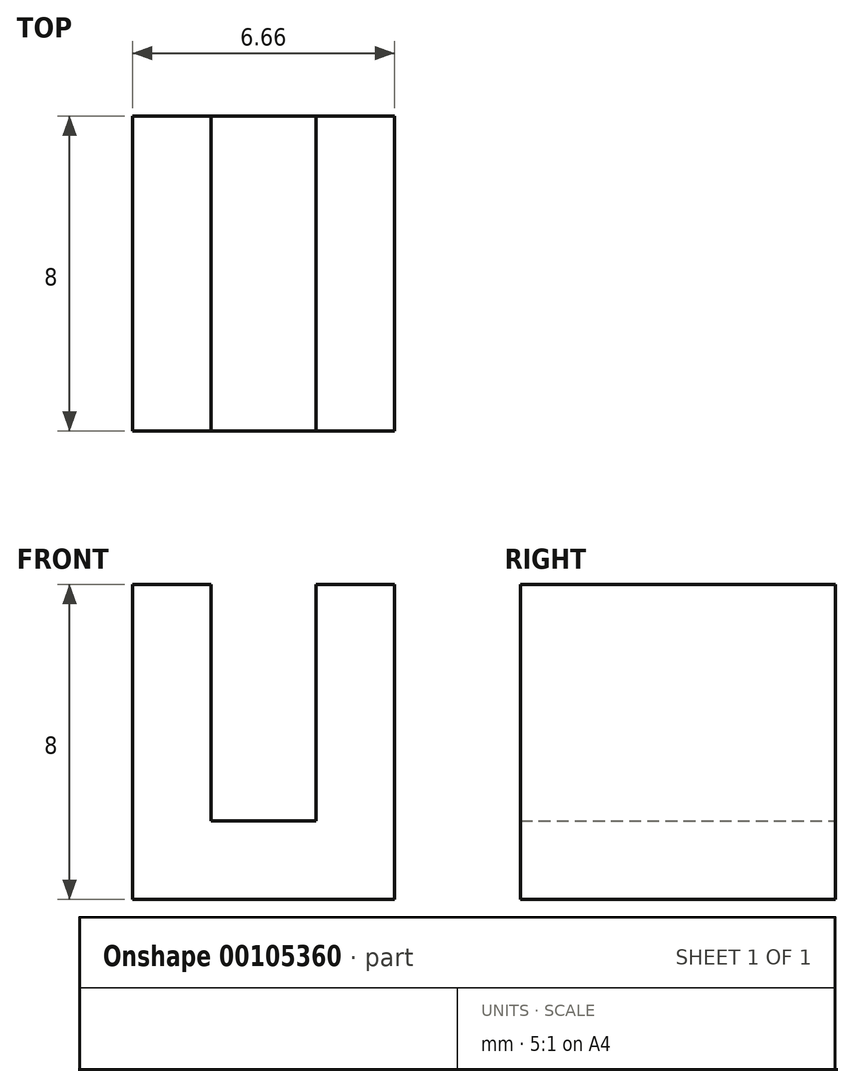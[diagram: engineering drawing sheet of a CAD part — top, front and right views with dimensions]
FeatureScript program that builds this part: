
annotation { "Feature Type Name" : "Feature", "Feature Type Description" : "" }
export const myFeature = defineFeature(function(context is Context, id is Id, definition is map)
    precondition{}
    {
        {
            var Q0;
            Q0=qCreatedBy(makeId("Front.planeOp"),FACE);
            var sketch = newSketch(context, id + "F0", { "sketchPlane" : qUnion([Q0])});
            skLineSegment(sketch, "E0", {"start": v(0, 0) * mm, "end": v(1.33, 0) * mm});
            skLineSegment(sketch, "E1", {"start": v(1.33, 0) * mm, "end": v(1.33, 6) * mm});
            skLineSegment(sketch, "E2", {"start": v(1.33, 6) * mm, "end": v(3.33, 6) * mm});
            skLineSegment(sketch, "E3", {"start": v(3.33, 6) * mm, "end": v(3.33, -2) * mm});
            skLineSegment(sketch, "E4", {"start": v(3.33, -2) * mm, "end": v(0, -2) * mm});
            skLineSegment(sketch, "E5.MirrorCS", {"start": v(-1.33, 6) * mm, "end": v(-3.33, 6) * mm});
            skLineSegment(sketch, "E6.MirrorCS", {"start": v(-3.33, 6) * mm, "end": v(-3.33, -2) * mm});
            skLineSegment(sketch, "E7.MirrorCS", {"start": v(-1.33, 0) * mm, "end": v(-1.33, 6) * mm});
            skLineSegment(sketch, "E8.MirrorCS", {"start": v(0, 0) * mm, "end": v(-1.33, 0) * mm});
            skLineSegment(sketch, "E9.MirrorCS", {"start": v(-3.33, -2) * mm, "end": v(0, -2) * mm});
            skSolve(sketch);
        }
        {
            var Q0;
            Q0 = qSketchRegion(id + "F0", true);
            extrude(context, id + "F1", {"entities" : qUnion([Q0]), "depth" : 8 * mm});
        }
    });
